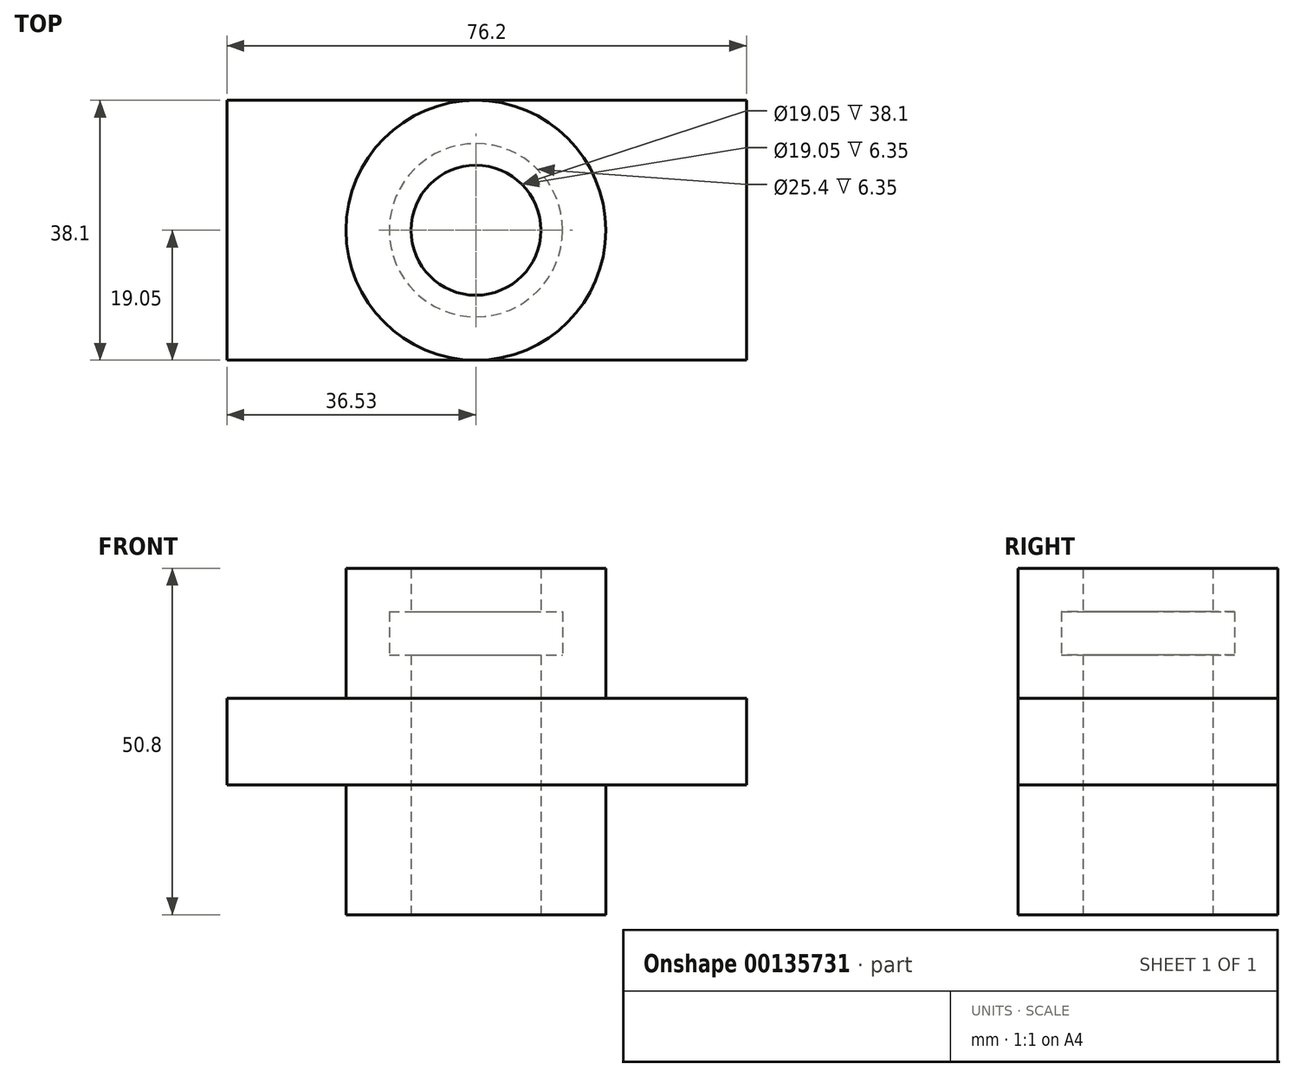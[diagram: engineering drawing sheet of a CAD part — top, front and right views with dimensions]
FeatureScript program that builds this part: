
annotation { "Feature Type Name" : "Feature", "Feature Type Description" : "" }
export const myFeature = defineFeature(function(context is Context, id is Id, definition is map)
    precondition{}
    {
        {
            var Q0;
            Q0=qCreatedBy(makeId("Front.planeOp"),FACE);
            var sketch = newSketch(context, id + "F0", { "sketchPlane" : qUnion([Q0])});
            skLineSegment(sketch, "E0", {"start": v(9.52, 0) * mm, "end": v(9.52, 38.1) * mm});
            skLineSegment(sketch, "E1", {"start": v(9.52, 38.1) * mm, "end": v(12.7, 38.1) * mm});
            skLineSegment(sketch, "E2", {"start": v(12.7, 38.1) * mm, "end": v(12.7, 44.45) * mm});
            skLineSegment(sketch, "E3", {"start": v(12.7, 44.45) * mm, "end": v(9.52, 44.45) * mm});
            skLineSegment(sketch, "E4", {"start": v(9.52, 44.45) * mm, "end": v(9.52, 50.8) * mm});
            skLineSegment(sketch, "E5", {"start": v(9.52, 50.8) * mm, "end": v(19.05, 50.8) * mm});
            skLineSegment(sketch, "E6", {"start": v(19.05, 50.8) * mm, "end": v(19.05, 0) * mm});
            skLineSegment(sketch, "E7", {"start": v(19.05, 0) * mm, "end": v(9.52, 0) * mm});
            skLineSegment(sketch, "E8", {"start": v(0, 0) * mm, "end": v(0, 50.8) * mm});
            skSolve(sketch);
        }
        {
            var Q0;
            Q0 = qSketchRegion(id + "F0", true);
            var Q1;
            Q1=sQuery(id+"F0.wireOp",EDGE,"E8");
            revolve(context, id + "F1", {"entities" : qUnion([Q0]), "axis" : qUnion([Q1]), "revolveType" : RevolveType.FULL});
        }
        {
            var Q0;
            Q0=qCreatedBy(makeId("Front.planeOp"),FACE);
            var sketch = newSketch(context, id + "F2", { "sketchPlane" : qUnion([Q0])});
            skLineSegment(sketch, "E9.bottom", {"start": v(-36.53, 31.75) * mm, "end": v(39.67, 31.75) * mm});
            skLineSegment(sketch, "E9.top", {"start": v(-36.53, 19.05) * mm, "end": v(39.67, 19.05) * mm});
            skLineSegment(sketch, "E9.left", {"start": v(-36.53, 31.75) * mm, "end": v(-36.53, 19.05) * mm});
            skLineSegment(sketch, "E9.right", {"start": v(39.67, 31.75) * mm, "end": v(39.67, 19.05) * mm});
            skSolve(sketch);
        }
        {
            var Q0;
            Q0 = qSketchRegion(id + "F2", true);
            extrude(context, id + "F3", {"entities" : qUnion([Q0]), "operationType" : NewBodyOperationType.ADD, "endBound" : BoundingType.SYMMETRIC, "depth" : 38.1 * mm});
        }
        {
            var Q0;
            Q0=makeQuery(id+"F3.boolean.opBoolean","SPLIT",FACE,{"disambiguationData":[TD([makeQuery(id+"F1.opRevolve","SWEPT_FACE",FACE,{"disambiguationData":[OSD([sQuery(id+"F0.wireOp",EDGE,"E0")])]})])],"derivedFrom":makeQuery(id+"F3.opExtrude","SWEPT_FACE",FACE,{"disambiguationData":[OSD([sQuery(id+"F2.wireOp",EDGE,"E9.bottom")])]})});
            var sketch = newSketch(context, id + "F4", { "sketchPlane" : qUnion([Q0])});
            skCircle(sketch, "E10", {"center": v(0, 0) * mm, "radius": 9.53 * mm});
            skSolve(sketch);
        }
        {
            var Q0;
            Q0 = qSketchRegion(id + "F4", true);
            extrude(context, id + "F5", {"entities" : qUnion([Q0]), "operationType" : NewBodyOperationType.REMOVE, "endBound" : BoundingType.THROUGH_ALL, "oppositeDirection" : true, "depth" : 25.4 * mm});
        }
    });
